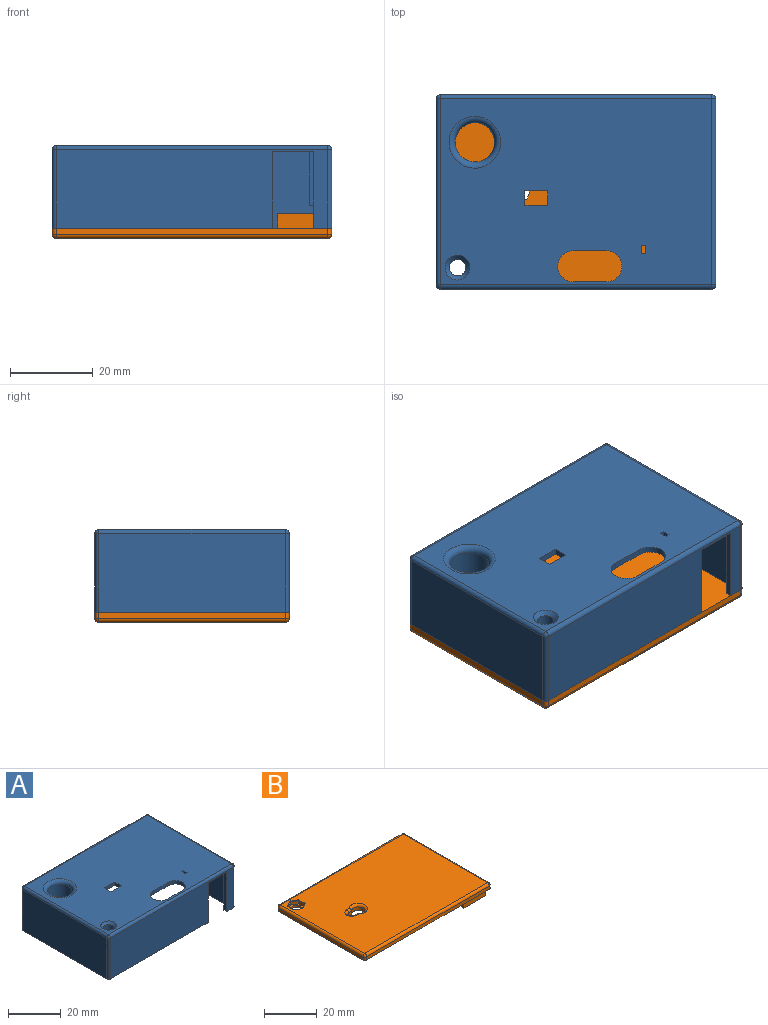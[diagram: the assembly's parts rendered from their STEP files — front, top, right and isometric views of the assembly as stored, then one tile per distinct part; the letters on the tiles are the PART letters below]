
ASSEMBLY  parts=2 mates=1
PART A: 64 faces, bbox 67.7x47x20 mm
  f0: plane 44.7x18.5mm, normal (0,1,0), area 666.8mm2, adj f3,f7,f24,f27,f29,f39,f40,f41
  f1: plane 65.7x19mm, normal (0,-1,0), area 1063.3mm2, adj f7,f24,f47,f48,f53,f59,f62
  f2: plane 37x18.5mm, normal (1,0,0), area 592.5mm2, adj f4,f7,f24,f26,f42,f43,f46
  f3: plane 6x1.5mm, normal (1,0,0), area 9mm2, adj f0,f24,f25,f40
  f4: plane 64.7x18.5mm, normal (0,-1,0), area 1092.9mm2, adj f2,f5,f7,f24,f33,f34,f35,f37
  f5: plane 44x18.5mm, normal (-1,0,0), area 528mm2, adj f4,f6,f7,f24,f30,f34
  f6: plane 18.5x3mm, normal (0,1,0), area 55.5mm2, adj f5,f7,f24,f48
  f7: plane 64.7x45.5mm, normal (0,0,-1), area 2448.6mm2, adj f0,f1,f2,f4,f5,f6,f8,f9
  f8: plane 5.5x1.5mm, normal (0,-1,0), area 8.2mm2, adj f7,f9,f17,f20
  f9: plane 3.5x1.5mm, normal (-1,0,0), area 5.2mm2, adj f7,f8,f10,f20
  f10: plane 5.5x1.5mm, normal (0,1,0), area 8.2mm2, adj f7,f9,f17,f20
  f11: plane 1.5x1mm, normal (0,1,0), area 1.5mm2, adj f7,f12,f18,f20
  f12: plane 2x1.5mm, normal (1,0,0), area 3mm2, adj f7,f11,f13,f20
  f13: plane 1.5x1mm, normal (0,-1,0), area 1.5mm2, adj f7,f12,f18,f20
  f14: plane 8x1.5mm, normal (0,-1,0), area 12mm2, adj f7,f15,f19,f20
  f15: cylinder r=3.75mm len=7.5mm, axis (0,0,1), area 17.7mm2, adj f7,f14,f16,f20
  f16: plane 8x1.5mm, normal (0,1,0), area 12mm2, adj f7,f15,f19,f20
  f17: plane 3.5x1.5mm, normal (1,0,0), area 5.2mm2, adj f7,f8,f10,f20
  f18: plane 2x1.5mm, normal (-1,0,0), area 3mm2, adj f7,f11,f13,f20
  f19: cylinder r=3.75mm len=7.5mm, axis (0,0,1), area 17.7mm2, adj f7,f14,f16,f20
  f20: plane 65.7x45mm, normal (0,0,1), area 2680.1mm2, adj f8,f9,f10,f11,f12,f13,f14,f15
  f21: plane 65.7x19mm, normal (0,1,0), area 1248.3mm2, adj f24,f51,f55,f56
  f22: plane 45x19mm, normal (-1,0,0), area 855mm2, adj f24,f51,f53,f54
  f23: plane 45x19mm, normal (1,0,0), area 855mm2, adj f24,f56,f60,f62
  f24: plane 67.7x47mm, normal (0,0,-1), area 355.5mm2, adj f0,f1,f2,f3,f4,f5,f6,f21
  f25: cylinder r=1mm len=18.5mm, axis (0,0,1), area 29.1mm2, adj f3,f7,f24,f26,f28
  f26: plane 18.5x6mm, normal (0,1,0), area 111mm2, adj f2,f7,f24,f25
  f27: plane 13x6mm, normal (1,0,0), area 78mm2, adj f0,f7,f28,f29
  f28: plane 17x10.7mm, normal (0,1,0), area 160.2mm2, adj f7,f25,f27,f29,f39,f40,f41
  f29: plane 6x3mm, normal (0,0,-1), area 18mm2, adj f0,f27,f28,f39
  f30: plane 13x1mm, normal (0,-1,0), area 13mm2, adj f5,f7,f31,f34
  f31: plane 20x13mm, normal (-1,0,0), area 260mm2, adj f7,f30,f32,f34
  f32: plane 13x3mm, normal (0,-1,0), area 39mm2, adj f7,f31,f33,f34
  f33: plane 13x2mm, normal (-1,0,0), area 26mm2, adj f4,f7,f32,f34
  f34: plane 22x4mm, normal (0,0,-1), area 28mm2, adj f4,f5,f30,f31,f32,f33
  f35: plane 13x1mm, normal (1,0,0), area 13mm2, adj f4,f7,f36,f38
  f36: plane 13x4mm, normal (0,-1,0), area 52mm2, adj f7,f35,f37,f38
  f37: plane 13x1mm, normal (-1,0,0), area 13mm2, adj f4,f7,f36,f38
  f38: plane 4x1mm, normal (0,0,-1), area 4mm2, adj f4,f35,f36,f37
  f39: plane 6x0.77mm, normal (1,0,0), area 4.6mm2, adj f0,f28,f29,f41
  f40: plane 7.01x6mm, normal (0.31,0,-0.95), area 44.2mm2, adj f0,f3,f28,f41
  f41: cylinder r=1mm len=6mm, axis (0,-1,0), area 7.5mm2, adj f0,f28,f39,f40
  f42: plane 8x7.9mm, normal (0,1,0), area 63.2mm2, adj f2,f7,f44,f46
  f43: plane 8x7.9mm, normal (0,-1,0), area 63.2mm2, adj f2,f7,f44,f46
  f44: cylinder r=5.75mm len=11.5mm, axis (0,0,1), area 144.5mm2, adj f7,f42,f43,f46
  f45: cylinder r=4.75mm len=9.5mm, axis (0,0,1), area 238.8mm2, adj f46,f63
  f46: plane 13.65x11.5mm, normal (0,0,-1), area 71.9mm2, adj f2,f42,f43,f44,f45
  f47: plane 18.5x1.5mm, normal (1,0,0), area 27.8mm2, adj f0,f1,f7,f24
  f48: plane 18.5x1.5mm, normal (-1,0,0), area 27.8mm2, adj f1,f6,f7,f24
  f49: cylinder r=2mm len=19mm, axis (0,0,1), area 238.8mm2, adj f24,f50
  f50: cone r=2mm half-angle=45deg, axis (0,0,1), area 22.2mm2, adj f20,f49
  f51: cylinder r=1mm len=19mm, axis (0,0,1), area 29.8mm2, adj f21,f22,f24,f52
  f52: sphere r=1mm, area 1.6mm2, adj f51,f54,f55
  f53: cylinder r=1mm len=19mm, axis (0,0,-1), area 29.8mm2, adj f1,f22,f24,f57
  f54: cylinder r=1mm len=45mm, axis (0,-1,0), area 70.7mm2, adj f20,f22,f52,f57
  f55: cylinder r=1mm len=65.7mm, axis (-1,0,0), area 103.2mm2, adj f20,f21,f52,f58
  f56: cylinder r=1mm len=19mm, axis (0,0,-1), area 29.8mm2, adj f21,f23,f24,f58
  f57: sphere r=1mm, area 1.6mm2, adj f53,f54,f59
  f58: sphere r=1mm, area 1.6mm2, adj f55,f56,f60
  f59: cylinder r=1mm len=65.7mm, axis (1,0,0), area 103.2mm2, adj f1,f20,f57,f61
  f60: cylinder r=1mm len=45mm, axis (0,1,0), area 70.7mm2, adj f20,f23,f58,f61
  f61: sphere r=1mm, area 1.6mm2, adj f59,f60,f62
  f62: cylinder r=1mm len=19mm, axis (0,0,1), area 29.8mm2, adj f1,f23,f24,f61
  f63: torus R=6.25mm, axis (0,0,1), area 78.4mm2, adj f20,f45
PART B: 55 faces, bbox 67.6x47x6 mm
  f0: plane 65.6x45mm, normal (0,0,1), area 2870.3mm2, adj f29,f30,f34,f35,f38,f39,f40,f41
  f1: plane 67.6x47mm, normal (0,0,-1), area 3074.3mm2, adj f2,f3,f4,f5,f6,f7,f8,f9
  f2: cylinder r=2mm len=4mm, axis (0,0,1), area 10.1mm2, adj f1,f19
  f3: plane 45x1.5mm, normal (1,0,0), area 67.5mm2, adj f1,f28,f34,f37
  f4: plane 65.6x1.5mm, normal (0,1,0), area 98.4mm2, adj f1,f31,f35,f37
  f5: plane 45x1.5mm, normal (-1,0,0), area 67.5mm2, adj f1,f26,f30,f31
  f6: plane 65.6x1.5mm, normal (0,-1,0), area 98.4mm2, adj f1,f26,f28,f29
  f7: plane 10x3.5mm, normal (-1,0,0), area 35mm2, adj f1,f8,f12,f13
  f8: plane 10x3.5mm, normal (0,1,0), area 35mm2, adj f1,f7,f9,f13
  f9: plane 3.5x1.5mm, normal (-1,0,0), area 5.2mm2, adj f1,f8,f10,f13
  f10: plane 11.5x3.5mm, normal (0,-1,0), area 40.3mm2, adj f1,f9,f11,f13
  f11: plane 11.5x3.5mm, normal (1,0,0), area 40.2mm2, adj f1,f10,f12,f13
  f12: plane 3.5x1.5mm, normal (0,1,0), area 5.3mm2, adj f1,f7,f11,f13
  f13: plane 11.5x11.5mm, normal (0,0,-1), area 32.2mm2, adj f7,f8,f9,f10,f11,f12
  f14: plane 6x3.5mm, normal (0,1,0), area 14.4mm2, adj f1,f15,f17,f18,f44,f45,f46
  f15: plane 5x1mm, normal (-1,0,0), area 5mm2, adj f14,f16,f18,f45
  f16: plane 6x3.5mm, normal (0,-1,0), area 14.4mm2, adj f1,f15,f17,f18,f44,f45,f46
  f17: plane 5x3.5mm, normal (1,0,0), area 17.5mm2, adj f1,f14,f16,f18
  f18: plane 5x2mm, normal (0,0,-1), area 10mm2, adj f14,f15,f16,f17
  f19: plane 6.35x5.5mm, normal (0,0,1), area 13.6mm2, adj f2,f20,f21,f22,f23,f24,f25
  f20: plane 2.75x1.59mm, normal (-0.5,-0.87,0), area 4.6mm2, adj f19,f21,f25,f39
  f21: plane 2.75x1.59mm, normal (0.5,-0.87,0), area 4.6mm2, adj f19,f20,f22,f38
  f22: plane 3.18x1.45mm, normal (1,0,0), area 4.6mm2, adj f19,f21,f23,f40
  f23: plane 2.75x1.59mm, normal (0.5,0.87,0), area 4.6mm2, adj f19,f22,f24,f42
  f24: plane 2.75x1.59mm, normal (-0.5,0.87,0), area 4.6mm2, adj f19,f23,f25,f43
  f25: plane 3.18x1.45mm, normal (-1,0,0), area 4.6mm2, adj f19,f20,f24,f41
  f26: cylinder r=1mm len=1.5mm, axis (0,0,-1), area 2.4mm2, adj f1,f5,f6,f27
  f27: sphere r=1mm, area 1.6mm2, adj f26,f29,f30
  f28: cylinder r=1mm len=1.5mm, axis (0,0,1), area 2.4mm2, adj f1,f3,f6,f32
  f29: cylinder r=1mm len=65.6mm, axis (-1,0,0), area 103mm2, adj f0,f6,f27,f32
  f30: cylinder r=1mm len=45mm, axis (0,1,0), area 70.7mm2, adj f0,f5,f27,f33
  f31: cylinder r=1mm len=1.5mm, axis (0,0,1), area 2.4mm2, adj f1,f4,f5,f33
  f32: sphere r=1mm, area 1.6mm2, adj f28,f29,f34
  f33: sphere r=1mm, area 1.6mm2, adj f30,f31,f35
  f34: cylinder r=1mm len=45mm, axis (0,-1,0), area 70.7mm2, adj f0,f3,f32,f36
  f35: cylinder r=1mm len=65.6mm, axis (1,0,0), area 103mm2, adj f0,f4,f33,f36
  f36: sphere r=1mm, area 1.6mm2, adj f34,f35,f37
  f37: cylinder r=1mm len=1.5mm, axis (0,0,-1), area 2.4mm2, adj f1,f3,f4,f36
  f38: cylinder r=0.25mm len=3.13mm, axis (0.87,0.5,0), area 1.3mm2, adj f0,f21,f39,f40
  f39: cylinder r=0.25mm len=3.13mm, axis (0.87,-0.5,0), area 1.3mm2, adj f0,f20,f38,f41
  f40: cylinder r=0.25mm len=3.46mm, axis (0,1,0), area 1.3mm2, adj f0,f22,f38,f42
  f41: cylinder r=0.25mm len=3.46mm, axis (0,-1,0), area 1.3mm2, adj f0,f25,f39,f43
  f42: cylinder r=0.25mm len=3.13mm, axis (-0.87,0.5,0), area 1.3mm2, adj f0,f23,f40,f43
  f43: cylinder r=0.25mm len=3.13mm, axis (-0.87,-0.5,0), area 1.3mm2, adj f0,f24,f41,f42
  f44: plane 5x0.77mm, normal (-1,0,0), area 3.8mm2, adj f1,f14,f16,f46
  f45: plane 5x1mm, normal (0,0,-1), area 5mm2, adj f14,f15,f16,f46
  f46: plane 5x3mm, normal (-0.5,0,-0.87), area 17.3mm2, adj f14,f16,f44,f45
  f47: cylinder r=7mm len=1.82mm, axis (0,0,1), area 2.8mm2, adj f1,f48,f50,f51
  f48: cylinder r=1.5mm len=3mm, axis (0,0,1), area 7.1mm2, adj f1,f47,f49,f53
  f49: cylinder r=7mm len=1.82mm, axis (0,0,1), area 2.8mm2, adj f1,f48,f50,f54
  f50: cylinder r=2.5mm len=5mm, axis (0,0,1), area 17.7mm2, adj f1,f47,f49,f52
  f51: torus R=6mm, axis (0,0,1), area 2.6mm2, adj f0,f47,f52,f53
  f52: torus R=3.5mm, axis (0,0,1), area 20.9mm2, adj f0,f50,f51,f54
  f53: torus R=2.5mm, axis (0,0,1), area 9.2mm2, adj f0,f48,f51,f54
  f54: torus R=6mm, axis (0,0,1), area 2.6mm2, adj f0,f49,f52,f53
PLACE A t=(2.63,0.13,-0.94)mm
PLACE B rot(axis=(1,0,0),180deg) t=(-4.77,0.13,-20.94)mm
MATE slider B.f2 <-> A.f49  axis (0,0,1) through (-33.37,-18.17,-20.94)mm
